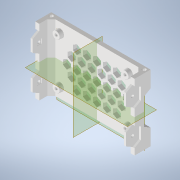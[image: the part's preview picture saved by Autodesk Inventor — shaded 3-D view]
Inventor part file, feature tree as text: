
AUTODESK INVENTOR PART (.ipt)
format: ipt  version: 2022.2 (Build 262287000, 287)  size: 735,232 bytes
history: native  units: mm
features: reference x17, extrude x13, sketch x13, projected_geometry x12, plane x3, chamfer x3, other x3, mirror x2, pattern_linear x2, shell x1, fillet x1
ambient origin geometry x8: Origin, YZ Plane, XZ Plane, XY Plane, X Axis, Y Axis, Z Axis, Center Point
bodies: Solid1 (feature_tree)
feature tree (70):
  plane  "Work Plane1"
  extrude  "Extrusion1"  Depth=4.0mm
  extrude  "Extrusion2"  Depth=8.0mm TaperAngle=45.0deg
  chamfer  "Chamfer1"  Distance=25.0mm
  shell  "Shell1"  Thickness=150.0deg
  extrude  "Extrusion5"  Depth=3.5mm
  extrude  "Extrusion6"  TaperAngle=60.0deg  [1 undecoded]
  extrude  "Extrusion8"  Depth=8.0mm
  extrude  "Extrusion10"  Depth=8.0mm
  extrude  "Extrusion11"  Depth=8.0mm
  extrude  "Extrusion17"  TaperAngle=60.0deg  [1 undecoded]
  extrude  "Extrusion7"  TaperAngle=60.0deg  [1 undecoded]
  plane  "Work Plane3"
  plane  "Work Plane4"
  mirror  "Mirror2"
  mirror  "Mirror3"
  chamfer  "Chamfer4"  Distance=10.0mm
  extrude  "Extrusion14"  TaperAngle=0.0deg  [1 undecoded]
  fillet  "Fillet3"  Radius=8.0mm
  extrude  "Extrusion16"  Depth=8.0mm
  pattern_linear  "Rectangular Pattern2"  Spacing1=12.0mm  [1 undecoded]
  pattern_linear  "Rectangular Pattern4"  Spacing1=12.0mm  [1 undecoded]
  extrude  "Extrusion18"  Depth=10.0mm
  extrude  "Extrusion15"  Depth=10.0mm
  chamfer  "Chamfer5"  Distance=10.0mm
  sketch  "Sketch3"  dims[d1=20.0mm d2=0.0mm d3=4.0mm]
  reference  "Reference1"
  reference  "Reference2"
  reference  "Reference3"
  reference  "Reference4"
  reference  "Reference5"
  reference  "Reference6"
  reference  "Reference7"
  reference  "Reference8"
  reference  "Reference9"
  reference  "Reference10"
  reference  "Reference11"
  reference  "Reference12"
  sketch  "Sketch4"  dims[d4=0.0mm d5=0.0mm d6=8.0mm d7=2.0mm d8=45.0deg]
  reference  "Reference13"
  sketch  "Sketch7"  dims[d9=5.0mm d27=25.0mm d28=0.0mm d29=150.0deg]
  projected_geometry  "Projected Loop2"
  sketch  "Sketch8"  dims[d30=20.0mm d31=0.0mm d37=3.5mm]
  projected_geometry  "Projected Loop3"
  sketch  "Sketch10"  dims[d38=12.0mm d39=0.436332mm d43=60.0deg]
  projected_geometry  "Projected Loop5"
  sketch  "Sketch12"  dims[d44=60.0deg d45=8.0mm]
  projected_geometry  "Projected Loop7"
  sketch  "Sketch15"  dims[d46=15.0mm d47=8.0mm]
  projected_geometry  "Projected Loop9"
  sketch  "Sketch16"  dims[d48=2.5mm d49=0.0mm d53=8.0mm]
  projected_geometry  "Projected Loop10"
  sketch  "Sketch19"  dims[d54=8.0mm d55=60.0deg]
  reference  "Reference14"
  reference  "Reference15"
  reference  "Reference16"
  reference  "Reference17"
  sketch  "Sketch20"  dims[d56=60.0deg d57=60.0deg]
  projected_geometry  "Projected Loop13"
  projected_geometry  "Projected Loop14"
  projected_geometry  "Projected Loop15"
  projected_geometry  "Projected Loop16"
  sketch  "Sketch21"  dims[d58=60.0deg d59=10.0mm d60=0.0mm]
  projected_geometry  "Projected Loop17"
  sketch  "Sketch22"  dims[d61=3.5mm d62=0.0mm d63=0.0mm]
  sketch  "Sketch23"  dims[d67=0.5mm d68=2.0mm d69=45.0deg d79=8.0mm d80=8.0mm d81=12.0mm d82=12.0mm d83=10.0mm d84=10.0mm d85=10.0mm d86=10.0mm d87=5.0mm d88=-0.872665mm d89=3.0mm d90=3.0mm d91=3.0mm d92=3.0mm d93=6.0mm d94=0.436332mm d95=0.5mm d96=2.0mm d97=45.0deg d98=0.5mm d101=0.0mm d102=0.0mm d106=5.75mm d107=5.75mm d108=0.5mm d109=0.0mm d113=10.0mm d114=70.0mm d116=12.5mm d120=10.0mm d122=30.0mm d124=22.0mm d125=0.0mm d126=0.0mm d127=22.0mm d128=3.0mm]
  projected_geometry  "Projected Loop18"
  other  "<userpath>\Desktop\Jetson-Nano-2GB-Case\A.iam"
  other  "A.iam"
  other  "A-00:1"
note: 6 required parameter values undecoded (feature->parameter linkage not recoverable at this tier; creation-order binding heuristic only, values carry confidence <= 0.55)
